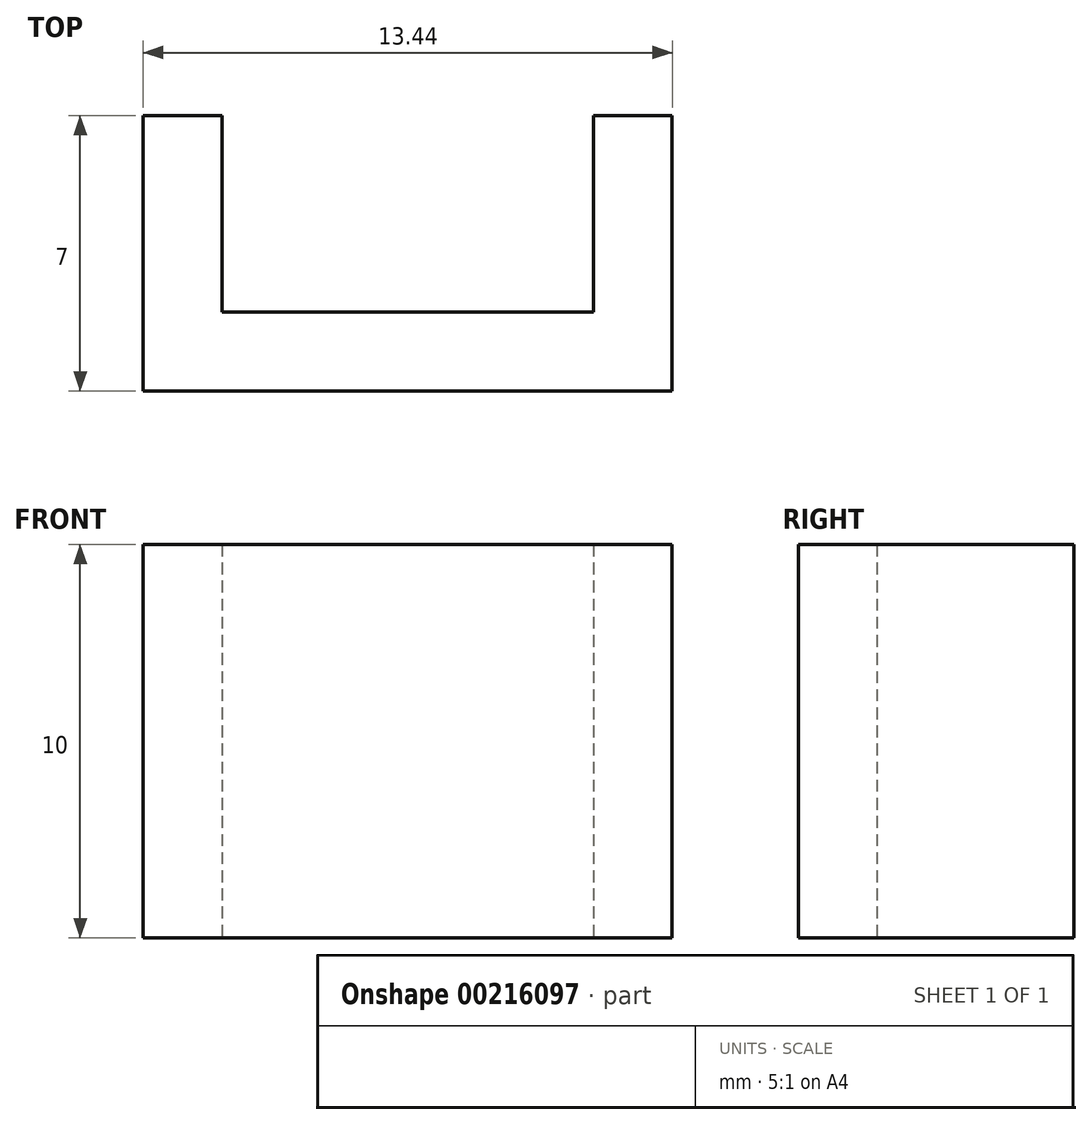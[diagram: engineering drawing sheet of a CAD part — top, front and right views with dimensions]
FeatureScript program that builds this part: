
annotation { "Feature Type Name" : "Feature", "Feature Type Description" : "" }
export const myFeature = defineFeature(function(context is Context, id is Id, definition is map)
    precondition{}
    {
        {
            var Q0;
            Q0=qCreatedBy(makeId("Top.planeOp"),FACE);
            var sketch = newSketch(context, id + "F0", { "sketchPlane" : qUnion([Q0])});
            skLineSegment(sketch, "E0", {"start": v(0, 0) * mm, "end": v(0, -5) * mm});
            skLineSegment(sketch, "E1", {"start": v(0, -5) * mm, "end": v(9.44, -5) * mm});
            skLineSegment(sketch, "E2", {"start": v(9.44, -5) * mm, "end": v(9.44, 0) * mm});
            skLineSegment(sketch, "E3", {"start": v(0, 0) * mm, "end": v(-2, 0) * mm});
            skLineSegment(sketch, "E4", {"start": v(-2, 0) * mm, "end": v(-2, -7) * mm});
            skLineSegment(sketch, "E5", {"start": v(-2, -7) * mm, "end": v(11.44, -7) * mm});
            skLineSegment(sketch, "E6", {"start": v(11.44, -7) * mm, "end": v(11.44, 0) * mm});
            skLineSegment(sketch, "E7", {"start": v(11.44, 0) * mm, "end": v(9.44, 0) * mm});
            skSolve(sketch);
        }
        {
            var Q0;
            Q0=makeQuery(id+"F0.imprint","IMPRINT",FACE,{"disambiguationData":[TD([[makeQuery(id+"F0.imprint","IMPRINT",EDGE,{"derivedFrom":sQuery(id+"F0.wireOp",EDGE,"E0")}),-1.0]])]});
            extrude(context, id + "F1", {"entities" : qUnion([Q0]), "depth" : 10 * mm});
        }
    });
